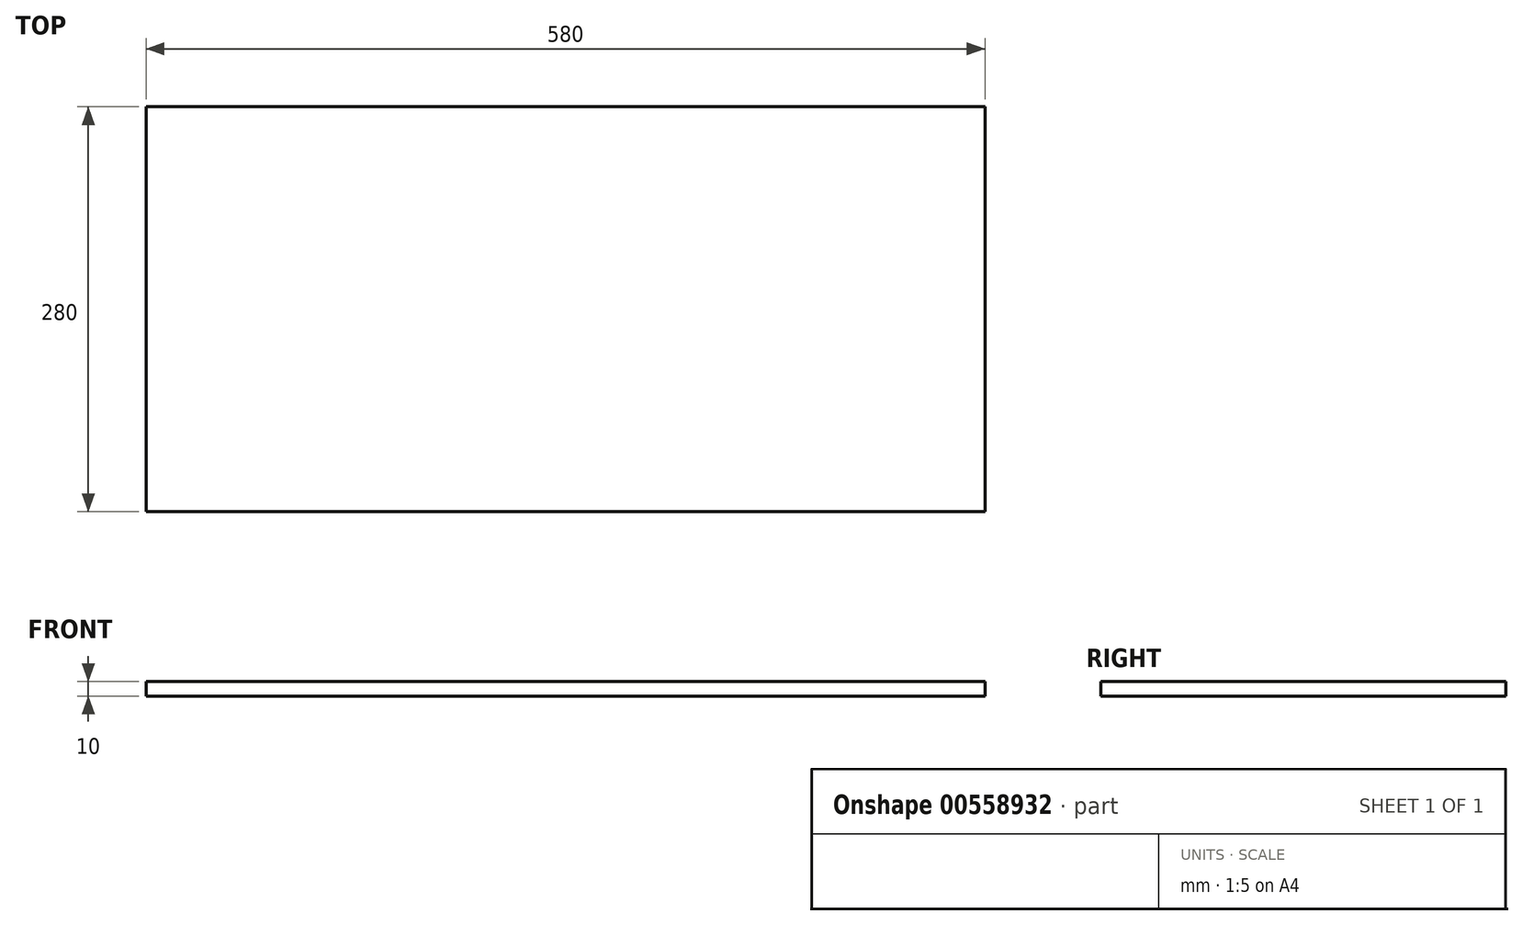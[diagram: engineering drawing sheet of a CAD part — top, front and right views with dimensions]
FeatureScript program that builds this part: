
annotation { "Feature Type Name" : "Feature", "Feature Type Description" : "" }
export const myFeature = defineFeature(function(context is Context, id is Id, definition is map)
    precondition{}
    {
        {
            var Q0;
            Q0=qCreatedBy(makeId("Top.planeOp"),FACE);
            var sketch = newSketch(context, id + "F0", { "sketchPlane" : qUnion([Q0])});
            skLineSegment(sketch, "E0.bottom", {"start": v(290, -140) * mm, "end": v(-290, -140) * mm});
            skLineSegment(sketch, "E0.top", {"start": v(290, 140) * mm, "end": v(-290, 140) * mm});
            skLineSegment(sketch, "E0.left", {"start": v(290, -140) * mm, "end": v(290, 140) * mm});
            skLineSegment(sketch, "E0.right", {"start": v(-290, -140) * mm, "end": v(-290, 140) * mm});
            skPoint(sketch, "E0.middle", {"position": v(0, 0) * mm});
            skSolve(sketch);
        }
        {
            var Q0;
            Q0=makeQuery(id+"F0.imprint","IMPRINT",FACE,{"disambiguationData":[TD([[makeQuery(id+"F0.imprint","IMPRINT",EDGE,{"derivedFrom":sQuery(id+"F0.wireOp",EDGE,"E0.bottom")}),-1.0]])]});
            extrude(context, id + "F1", {"entities" : qUnion([Q0]), "depth" : 10 * mm, "offsetDistance" : 25 * mm});
        }
    });
